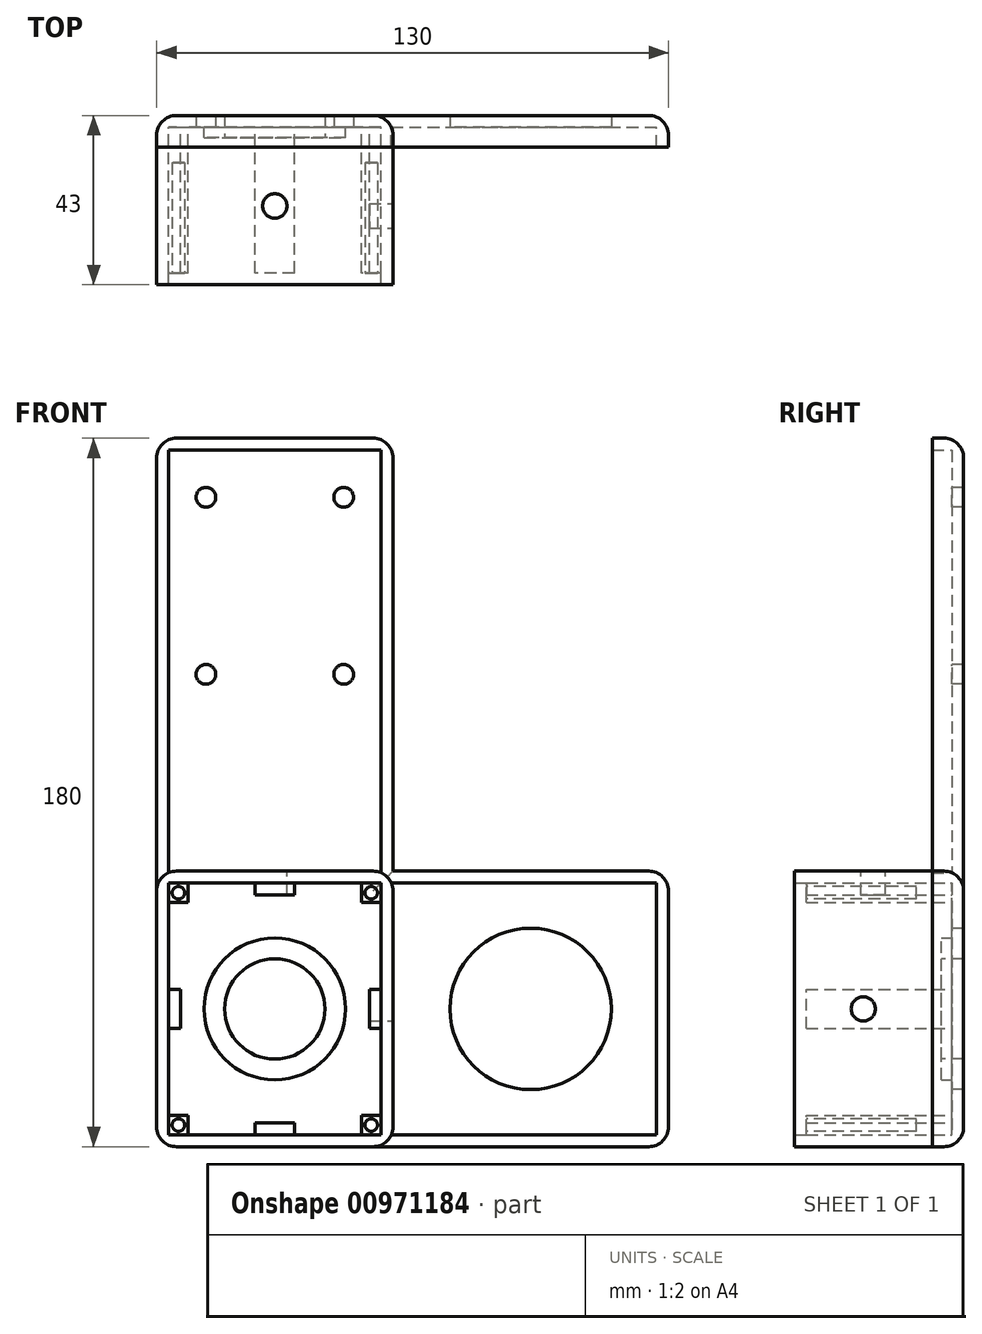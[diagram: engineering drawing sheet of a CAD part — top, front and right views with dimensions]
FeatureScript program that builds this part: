
annotation { "Feature Type Name" : "Feature", "Feature Type Description" : "" }
export const myFeature = defineFeature(function(context is Context, id is Id, definition is map)
    precondition{}
    {
        {
            var Q0;
            Q0=qCreatedBy(makeId("Front.planeOp"),FACE);
            var sketch = newSketch(context, id + "F0", { "sketchPlane" : qUnion([Q0])});
            skLineSegment(sketch, "E0.bottom", {"start": v(30, -90) * mm, "end": v(-30, -90) * mm});
            skLineSegment(sketch, "E0.top", {"start": v(30, 90) * mm, "end": v(-30, 90) * mm});
            skLineSegment(sketch, "E0.left", {"start": v(30, -90) * mm, "end": v(30, 90) * mm});
            skLineSegment(sketch, "E0.right", {"start": v(-30, -90) * mm, "end": v(-30, 90) * mm});
            skPoint(sketch, "E0.middle", {"position": v(0, 0) * mm});
            skCircle(sketch, "E1", {"center": v(0, -55) * mm, "radius": 12.75 * mm});
            skCircle(sketch, "E2", {"center": v(-17.5, 75) * mm, "radius": 2.5 * mm});
            skCircle(sketch, "E3", {"center": v(17.5, 75) * mm, "radius": 2.5 * mm});
            skCircle(sketch, "E4", {"center": v(-17.5, 30) * mm, "radius": 2.5 * mm});
            skCircle(sketch, "E5", {"center": v(17.5, 30) * mm, "radius": 2.5 * mm});
            skSolve(sketch);
        }
        {
            var Q0;
            Q0=makeQuery(id+"F0.imprint","IMPRINT",FACE,{"disambiguationData":[TD([[makeQuery(id+"F0.imprint","IMPRINT",EDGE,{"derivedFrom":sQuery(id+"F0.wireOp",EDGE,"E0.bottom")}),-1.0]])]});
            extrude(context, id + "F1", {"entities" : qUnion([Q0]), "oppositeDirection" : true, "depth" : 3 * mm, "offsetDistance" : 25 * mm});
        }
        {
            var Q0;
            Q0=makeQuery(id+"F1.opExtrude","CAP_FACE",FACE,{"disambiguationData":[OSD([sQuery(id+"F0.wireOp",EDGE,"E0.bottom"),sQuery(id+"F0.wireOp",EDGE,"E0.top"),sQuery(id+"F0.wireOp",EDGE,"E0.left"),sQuery(id+"F0.wireOp",EDGE,"E0.right"),sQuery(id+"F0.wireOp",EDGE,"E1")])],"isStart":true});
            var sketch = newSketch(context, id + "F2", { "sketchPlane" : qUnion([Q0])});
            skCircle(sketch, "E6", {"center": v(0, -55) * mm, "radius": 18 * mm});
            skSolve(sketch);
        }
        {
            var Q0;
            Q0=makeQuery(id+"F2.imprint","IMPRINT",FACE,{"disambiguationData":[TD([[makeQuery(id+"F2.imprint","IMPRINT",EDGE,{"derivedFrom":sQuery(id+"F2.wireOp",EDGE,"E6")}),1.0]])]});
            extrude(context, id + "F3", {"entities" : qUnion([Q0]), "operationType" : NewBodyOperationType.ADD, "depth" : 2.6 * mm, "offsetDistance" : 25 * mm});
        }
        {
            var Q0;
            Q0=makeQuery(id+"F1.opExtrude","CAP_FACE",FACE,{"disambiguationData":[OSD([sQuery(id+"F0.wireOp",EDGE,"E0.bottom"),sQuery(id+"F0.wireOp",EDGE,"E0.top"),sQuery(id+"F0.wireOp",EDGE,"E0.left"),sQuery(id+"F0.wireOp",EDGE,"E0.right"),sQuery(id+"F0.wireOp",EDGE,"E1")])],"isStart":true});
            var sketch = newSketch(context, id + "F4", { "sketchPlane" : qUnion([Q0])});
            skLineSegment(sketch, "E7.bottom", {"start": v(-30, -90) * mm, "end": v(30, -90) * mm});
            skLineSegment(sketch, "E7.top", {"start": v(-30, -20) * mm, "end": v(30, -20) * mm});
            skLineSegment(sketch, "E7.left", {"start": v(-30, -90) * mm, "end": v(-30, -20) * mm});
            skLineSegment(sketch, "E7.right", {"start": v(30, -90) * mm, "end": v(30, -20) * mm});
            skPoint(sketch, "E8", {"position": v(30, 0) * mm});
            skLineSegment(sketch, "E9", {"start": v(-27, -23) * mm, "end": v(27, -23) * mm});
            skLineSegment(sketch, "E10", {"start": v(27, -23) * mm, "end": v(27, -87) * mm});
            skLineSegment(sketch, "E11", {"start": v(27, -87) * mm, "end": v(-27, -87) * mm});
            skLineSegment(sketch, "E12", {"start": v(-27, -87) * mm, "end": v(-27, -23) * mm});
            skSolve(sketch);
        }
        {
            var Q0;
            Q0=makeQuery(id+"F4.imprint","IMPRINT",FACE,{"disambiguationData":[TD([[makeQuery(id+"F4.imprint","IMPRINT",EDGE,{"derivedFrom":sQuery(id+"F4.wireOp",EDGE,"E7.bottom")}),-1.0]])]});
            extrude(context, id + "F5", {"entities" : qUnion([Q0]), "operationType" : NewBodyOperationType.ADD, "depth" : 40 * mm, "offsetDistance" : 25 * mm});
        }
        {
            var Q0;
            Q0=makeQuery(id+"F5.boolean.opBoolean","SPLIT",FACE,{"disambiguationData":[TD([makeQuery(id+"F3.opExtrude","SWEPT_FACE",FACE,{"disambiguationData":[OSD([sQuery(id+"F2.wireOp",EDGE,"E6")])]})])],"derivedFrom":makeQuery(id+"F1.opExtrude","CAP_FACE",FACE,{"disambiguationData":[OSD([sQuery(id+"F0.wireOp",EDGE,"E0.bottom"),sQuery(id+"F0.wireOp",EDGE,"E0.top"),sQuery(id+"F0.wireOp",EDGE,"E0.left"),sQuery(id+"F0.wireOp",EDGE,"E0.right"),sQuery(id+"F0.wireOp",EDGE,"E1")])],"isStart":true})});
            var sketch = newSketch(context, id + "F6", { "sketchPlane" : qUnion([Q0])});
            skLineSegment(sketch, "E13.bottom", {"start": v(27, -23) * mm, "end": v(22, -23) * mm});
            skLineSegment(sketch, "E13.top", {"start": v(27, -28) * mm, "end": v(22, -28) * mm});
            skLineSegment(sketch, "E13.left", {"start": v(27, -23) * mm, "end": v(27, -28) * mm});
            skLineSegment(sketch, "E13.right", {"start": v(22, -23) * mm, "end": v(22, -28) * mm});
            skLineSegment(sketch, "E14.bottom", {"start": v(-27, -23) * mm, "end": v(-22, -23) * mm});
            skLineSegment(sketch, "E14.top", {"start": v(-27, -28) * mm, "end": v(-22, -28) * mm});
            skLineSegment(sketch, "E14.left", {"start": v(-27, -23) * mm, "end": v(-27, -28) * mm});
            skLineSegment(sketch, "E14.right", {"start": v(-22, -23) * mm, "end": v(-22, -28) * mm});
            skLineSegment(sketch, "E15.bottom", {"start": v(-27, -87) * mm, "end": v(-22, -87) * mm});
            skLineSegment(sketch, "E15.top", {"start": v(-27, -82) * mm, "end": v(-22, -82) * mm});
            skLineSegment(sketch, "E15.left", {"start": v(-27, -87) * mm, "end": v(-27, -82) * mm});
            skLineSegment(sketch, "E15.right", {"start": v(-22, -87) * mm, "end": v(-22, -82) * mm});
            skLineSegment(sketch, "E16.bottom", {"start": v(27, -87) * mm, "end": v(22, -87) * mm});
            skLineSegment(sketch, "E16.top", {"start": v(27, -82) * mm, "end": v(22, -82) * mm});
            skLineSegment(sketch, "E16.left", {"start": v(27, -87) * mm, "end": v(27, -82) * mm});
            skLineSegment(sketch, "E16.right", {"start": v(22, -87) * mm, "end": v(22, -82) * mm});
            skLineSegment(sketch, "E17.bottom", {"start": v(-5, -23) * mm, "end": v(5, -23) * mm});
            skLineSegment(sketch, "E17.top", {"start": v(-5, -26) * mm, "end": v(5, -26) * mm});
            skLineSegment(sketch, "E17.left", {"start": v(-5, -23) * mm, "end": v(-5, -26) * mm});
            skLineSegment(sketch, "E17.right", {"start": v(5, -23) * mm, "end": v(5, -26) * mm});
            skLineSegment(sketch, "E18.bottom", {"start": v(-5, -87) * mm, "end": v(5, -87) * mm});
            skLineSegment(sketch, "E18.top", {"start": v(-5, -84) * mm, "end": v(5, -84) * mm});
            skLineSegment(sketch, "E18.left", {"start": v(-5, -87) * mm, "end": v(-5, -84) * mm});
            skLineSegment(sketch, "E18.right", {"start": v(5, -87) * mm, "end": v(5, -84) * mm});
            skLineSegment(sketch, "E19.bottom", {"start": v(27, -50) * mm, "end": v(24, -50) * mm});
            skLineSegment(sketch, "E19.top", {"start": v(27, -60) * mm, "end": v(24, -60) * mm});
            skLineSegment(sketch, "E19.left", {"start": v(27, -50) * mm, "end": v(27, -60) * mm});
            skLineSegment(sketch, "E19.right", {"start": v(24, -50) * mm, "end": v(24, -60) * mm});
            skLineSegment(sketch, "E20.bottom", {"start": v(-27, -50) * mm, "end": v(-24, -50) * mm});
            skLineSegment(sketch, "E20.top", {"start": v(-27, -60) * mm, "end": v(-24, -60) * mm});
            skLineSegment(sketch, "E20.left", {"start": v(-27, -50) * mm, "end": v(-27, -60) * mm});
            skLineSegment(sketch, "E20.right", {"start": v(-24, -50) * mm, "end": v(-24, -60) * mm});
            skLineSegment(sketch, "E21", {"start": v(0, -33.43) * mm, "end": v(0, -77.94) * mm, "construction": true});
            skSolve(sketch);
        }
        {
            var Q0;
            Q0=makeQuery(id+"F6.imprint","IMPRINT",FACE,{"disambiguationData":[TD([[makeQuery(id+"F6.imprint","IMPRINT",EDGE,{"derivedFrom":sQuery(id+"F6.wireOp",EDGE,"E14.bottom")}),-1.0]])]});
            var Q1;
            Q1=makeQuery(id+"F6.imprint","IMPRINT",FACE,{"disambiguationData":[TD([[makeQuery(id+"F6.imprint","IMPRINT",EDGE,{"derivedFrom":sQuery(id+"F6.wireOp",EDGE,"E17.bottom")}),-1.0]])]});
            var Q2;
            Q2=makeQuery(id+"F6.imprint","IMPRINT",FACE,{"disambiguationData":[TD([[makeQuery(id+"F6.imprint","IMPRINT",EDGE,{"derivedFrom":sQuery(id+"F6.wireOp",EDGE,"E13.bottom")}),-1.0]])]});
            var Q3;
            Q3=makeQuery(id+"F6.imprint","IMPRINT",FACE,{"disambiguationData":[TD([[makeQuery(id+"F6.imprint","IMPRINT",EDGE,{"derivedFrom":sQuery(id+"F6.wireOp",EDGE,"E19.bottom")}),1.0]])]});
            var Q4;
            Q4=makeQuery(id+"F6.imprint","IMPRINT",FACE,{"disambiguationData":[TD([[makeQuery(id+"F6.imprint","IMPRINT",EDGE,{"derivedFrom":sQuery(id+"F6.wireOp",EDGE,"E20.bottom")}),-1.0]])]});
            var Q5;
            Q5=makeQuery(id+"F6.imprint","IMPRINT",FACE,{"disambiguationData":[TD([[makeQuery(id+"F6.imprint","IMPRINT",EDGE,{"derivedFrom":sQuery(id+"F6.wireOp",EDGE,"E16.bottom")}),-1.0]])]});
            var Q6;
            Q6=makeQuery(id+"F6.imprint","IMPRINT",FACE,{"disambiguationData":[TD([[makeQuery(id+"F6.imprint","IMPRINT",EDGE,{"derivedFrom":sQuery(id+"F6.wireOp",EDGE,"E18.bottom")}),-1.0]])]});
            var Q7;
            Q7=makeQuery(id+"F6.imprint","IMPRINT",FACE,{"disambiguationData":[TD([[makeQuery(id+"F6.imprint","IMPRINT",EDGE,{"derivedFrom":sQuery(id+"F6.wireOp",EDGE,"E15.bottom")}),-1.0]])]});
            extrude(context, id + "F7", {"entities" : qUnion([Q0, Q1, Q2, Q3, Q4, Q5, Q6, Q7]), "operationType" : NewBodyOperationType.ADD, "depth" : 37 * mm, "offsetDistance" : 25 * mm});
        }
        {
            var Q0;
            Q0=makeQuery(id+"F7.opExtrude","CAP_FACE",FACE,{"disambiguationData":[OSD([sQuery(id+"F6.wireOp",EDGE,"E13.bottom"),sQuery(id+"F6.wireOp",EDGE,"E13.top"),sQuery(id+"F6.wireOp",EDGE,"E13.left"),sQuery(id+"F6.wireOp",EDGE,"E13.right")])],"isStart":false});
            var sketch = newSketch(context, id + "F8", { "sketchPlane" : qUnion([Q0])});
            skCircle(sketch, "E22", {"center": v(24.5, -25.5) * mm, "radius": 1.6 * mm});
            skCircle(sketch, "E23", {"center": v(-24.5, -25.5) * mm, "radius": 1.6 * mm});
            skCircle(sketch, "E24", {"center": v(-24.5, -84.5) * mm, "radius": 1.6 * mm});
            skCircle(sketch, "E25", {"center": v(24.5, -84.5) * mm, "radius": 1.6 * mm});
            skSolve(sketch);
        }
        {
            var Q0;
            Q0=makeQuery(id+"F8.imprint","IMPRINT",FACE,{"disambiguationData":[TD([[makeQuery(id+"F8.imprint","IMPRINT",EDGE,{"derivedFrom":sQuery(id+"F8.wireOp",EDGE,"E22")}),1.0]])]});
            var Q1;
            Q1=makeQuery(id+"F8.imprint","IMPRINT",FACE,{"disambiguationData":[TD([[makeQuery(id+"F8.imprint","IMPRINT",EDGE,{"derivedFrom":sQuery(id+"F8.wireOp",EDGE,"E23")}),1.0]])]});
            var Q2;
            Q2=makeQuery(id+"F8.imprint","IMPRINT",FACE,{"disambiguationData":[TD([[makeQuery(id+"F8.imprint","IMPRINT",EDGE,{"derivedFrom":sQuery(id+"F8.wireOp",EDGE,"E25")}),1.0]])]});
            var Q3;
            Q3=makeQuery(id+"F8.imprint","IMPRINT",FACE,{"disambiguationData":[TD([[makeQuery(id+"F8.imprint","IMPRINT",EDGE,{"derivedFrom":sQuery(id+"F8.wireOp",EDGE,"E24")}),1.0]])]});
            extrude(context, id + "F9", {"entities" : qUnion([Q0, Q1, Q2, Q3]), "operationType" : NewBodyOperationType.REMOVE, "oppositeDirection" : true, "depth" : 28 * mm, "offsetDistance" : 25 * mm});
        }
        {
            var Q0;
            Q0=makeQuery(id+"F5.boolean.opBoolean","MERGE",FACE,{"derivedFrom":[makeQuery(id+"F1.opExtrude","SWEPT_FACE",FACE,{"disambiguationData":[OSD([sQuery(id+"F0.wireOp",EDGE,"E0.left")])]}),makeQuery(id+"F5.opExtrude","SWEPT_FACE",FACE,{"disambiguationData":[OSD([sQuery(id+"F4.wireOp",EDGE,"E7.right")])]})]});
            var sketch = newSketch(context, id + "F10", { "sketchPlane" : qUnion([Q0])});
            skLineSegment(sketch, "E26.bottom", {"start": v(3, -90) * mm, "end": v(0, -90) * mm});
            skLineSegment(sketch, "E26.top", {"start": v(3, -20) * mm, "end": v(0, -20) * mm});
            skLineSegment(sketch, "E26.left", {"start": v(3, -90) * mm, "end": v(3, -20) * mm});
            skLineSegment(sketch, "E26.right", {"start": v(0, -90) * mm, "end": v(0, -20) * mm});
            skSolve(sketch);
        }
        {
            var Q0;
            Q0=makeQuery(id+"F10.imprint","IMPRINT",FACE,{"disambiguationData":[TD([[makeQuery(id+"F10.imprint","IMPRINT",EDGE,{"derivedFrom":sQuery(id+"F10.wireOp",EDGE,"E26.bottom")}),-1.0]])]});
            extrude(context, id + "F11", {"entities" : qUnion([Q0]), "operationType" : NewBodyOperationType.ADD, "depth" : 70 * mm, "offsetDistance" : 25 * mm});
        }
        {
            var Q0;
            Q0=makeQuery(id+"F11.opExtrude","SWEPT_FACE",FACE,{"disambiguationData":[OSD([sQuery(id+"F10.wireOp",EDGE,"E26.right")])]});
            var sketch = newSketch(context, id + "F12", { "sketchPlane" : qUnion([Q0])});
            skLineSegment(sketch, "E27", {"start": v(30, -55) * mm, "end": v(128.66, -55) * mm, "construction": true});
            skPoint(sketch, "E27.endSnap0", {"position": v(100, -55) * mm});
            skLineSegment(sketch, "E28", {"start": v(65, 0) * mm, "end": v(65, -99.6) * mm, "construction": true});
            skPoint(sketch, "E28.startSnap0", {"position": v(65, -20) * mm});
            skSolve(sketch);
        }
        {
            var Q0;
            {var subQ0=sQuery(id+"F10.wireOp",EDGE,"E26.right");Q0=makeQuery(id+"F12.imprint","IMPRINT",FACE,{"disambiguationData":[TD([[makeQuery(id+"F12.imprint","IMPRINT",EDGE,{"derivedFrom":makeQuery(id+"F11.opExtrude","CAP_EDGE",EDGE,{"disambiguationData":[OSD([subQ0])],"isStart":false})}),1.0]])]});}
            var sketch = newSketch(context, id + "F13", { "sketchPlane" : qUnion([Q0])});
            skCircle(sketch, "E29", {"center": v(65, -55) * mm, "radius": 20.5 * mm});
            skSolve(sketch);
        }
        {
            var Q0;
            Q0=makeQuery(id+"F13.imprint","IMPRINT",FACE,{"disambiguationData":[TD([[makeQuery(id+"F13.imprint","IMPRINT",EDGE,{"derivedFrom":sQuery(id+"F13.wireOp",EDGE,"E29")}),1.0]])]});
            extrude(context, id + "F14", {"entities" : qUnion([Q0]), "operationType" : NewBodyOperationType.REMOVE, "endBound" : BoundingType.UP_TO_NEXT, "oppositeDirection" : true, "depth" : 25 * mm, "offsetDistance" : 25 * mm});
        }
        {
            var Q0;
            {var subQ0=sQuery(id+"F10.wireOp",EDGE,"E26.right");Q0=makeQuery(id+"F12.imprint","IMPRINT",FACE,{"disambiguationData":[TD([[makeQuery(id+"F12.imprint","IMPRINT",EDGE,{"derivedFrom":makeQuery(id+"F11.opExtrude","CAP_EDGE",EDGE,{"disambiguationData":[OSD([subQ0])],"isStart":false})}),1.0]])]});}
            var sketch = newSketch(context, id + "F15", { "sketchPlane" : qUnion([Q0])});
            skLineSegment(sketch, "E30.bottom", {"start": v(30, -20) * mm, "end": v(100, -20) * mm});
            skLineSegment(sketch, "E30.top", {"start": v(30, -23) * mm, "end": v(97, -23) * mm});
            skLineSegment(sketch, "E30.left", {"start": v(30, -20) * mm, "end": v(30, -23) * mm});
            skLineSegment(sketch, "E30.right", {"start": v(100, -20) * mm, "end": v(100, -23) * mm});
            skLineSegment(sketch, "E31.bottom", {"start": v(30, -87) * mm, "end": v(97, -87) * mm});
            skLineSegment(sketch, "E31.top", {"start": v(30, -90) * mm, "end": v(100, -90) * mm});
            skLineSegment(sketch, "E31.left", {"start": v(30, -87) * mm, "end": v(30, -90) * mm});
            skLineSegment(sketch, "E31.right", {"start": v(100, -87) * mm, "end": v(100, -90) * mm});
            skLineSegment(sketch, "E32.left", {"start": v(100, -23) * mm, "end": v(100, -87) * mm});
            skLineSegment(sketch, "E32.right", {"start": v(97, -23) * mm, "end": v(97, -87) * mm});
            skSolve(sketch);
        }
        {
            var Q0;
            Q0=makeQuery(id+"F15.imprint","IMPRINT",FACE,{"disambiguationData":[TD([[makeQuery(id+"F15.imprint","IMPRINT",EDGE,{"derivedFrom":sQuery(id+"F15.wireOp",EDGE,"E30.bottom")}),1.0]])]});
            extrude(context, id + "F16", {"entities" : qUnion([Q0]), "operationType" : NewBodyOperationType.ADD, "depth" : 5 * mm, "offsetDistance" : 25 * mm});
        }
        {
            var Q0;
            {var subQ1=sQuery(id+"F0.wireOp",EDGE,"E0.left");var subQ2=makeQuery(id+"F1.opExtrude","SWEPT_FACE",FACE,{"disambiguationData":[OSD([subQ1])]});var subQ3=sQuery(id+"F0.wireOp",EDGE,"E0.bottom");var subQ4=sQuery(id+"F4.wireOp",EDGE,"E7.right");var subQ5=makeQuery(id+"F5.opExtrude","SWEPT_FACE",FACE,{"disambiguationData":[OSD([subQ4])]});Q0=makeQuery(id+"F11.boolean.opBoolean","SPLIT",FACE,{"disambiguationData":[TD([makeQuery(id+"F1.opExtrude","SWEPT_FACE",FACE,{"disambiguationData":[OSD([subQ3])]})])],"derivedFrom":makeQuery(id+"F5.boolean.opBoolean","MERGE",FACE,{"derivedFrom":[subQ2,subQ5]})});}
            var sketch = newSketch(context, id + "F17", { "sketchPlane" : qUnion([Q0])});
            skCircle(sketch, "E33", {"center": v(-22.5, -55) * mm, "radius": 3.07 * mm});
            skPoint(sketch, "E33.centerSnap0", {"position": v(-22.5, -20) * mm});
            skSolve(sketch);
        }
        {
            var Q0;
            Q0=makeQuery(id+"F17.imprint","IMPRINT",FACE,{"disambiguationData":[TD([[makeQuery(id+"F17.imprint","IMPRINT",EDGE,{"derivedFrom":sQuery(id+"F17.wireOp",EDGE,"E33")}),1.0]])]});
            extrude(context, id + "F18", {"entities" : qUnion([Q0]), "operationType" : NewBodyOperationType.REMOVE, "endBound" : BoundingType.UP_TO_NEXT, "oppositeDirection" : true, "depth" : 25 * mm, "offsetDistance" : 25 * mm});
        }
        {
            var Q0;
            Q0=makeQuery(id+"F16.boolean.opBoolean","MERGE",FACE,{"derivedFrom":[makeQuery(id+"F5.opExtrude","SWEPT_FACE",FACE,{"disambiguationData":[OSD([sQuery(id+"F4.wireOp",EDGE,"E7.top")])]}),makeQuery(id+"F11.opExtrude","SWEPT_FACE",FACE,{"disambiguationData":[OSD([sQuery(id+"F10.wireOp",EDGE,"E26.top")])]}),makeQuery(id+"F16.opExtrude","SWEPT_FACE",FACE,{"disambiguationData":[OSD([sQuery(id+"F15.wireOp",EDGE,"E30.bottom")])]})]});
            var sketch = newSketch(context, id + "F19", { "sketchPlane" : qUnion([Q0])});
            skCircle(sketch, "E34", {"center": v(0, -20) * mm, "radius": 3.1 * mm});
            skPoint(sketch, "E34.centerSnap0", {"position": v(-30, -20) * mm});
            skSolve(sketch);
        }
        {
            var Q0;
            Q0=makeQuery(id+"F19.imprint","IMPRINT",FACE,{"disambiguationData":[TD([[makeQuery(id+"F19.imprint","IMPRINT",EDGE,{"derivedFrom":sQuery(id+"F19.wireOp",EDGE,"E34")}),1.0]])]});
            extrude(context, id + "F20", {"entities" : qUnion([Q0]), "operationType" : NewBodyOperationType.REMOVE, "endBound" : BoundingType.UP_TO_NEXT, "oppositeDirection" : true, "depth" : 25 * mm, "offsetDistance" : 25 * mm});
        }
        {
            var Q0;
            {var subQ0=sQuery(id+"F0.wireOp",EDGE,"E0.right");var subQ1=sQuery(id+"F0.wireOp",EDGE,"E0.left");var subQ2=sQuery(id+"F0.wireOp",EDGE,"E0.top");Q0=makeQuery(id+"F5.boolean.opBoolean","SPLIT",FACE,{"disambiguationData":[TD([makeQuery(id+"F1.opExtrude","SWEPT_FACE",FACE,{"disambiguationData":[OSD([subQ2])]})])],"derivedFrom":makeQuery(id+"F1.opExtrude","CAP_FACE",FACE,{"disambiguationData":[OSD([sQuery(id+"F0.wireOp",EDGE,"E0.bottom"),subQ2,subQ1,subQ0,sQuery(id+"F0.wireOp",EDGE,"E1")])],"isStart":true})});}
            var sketch = newSketch(context, id + "F21", { "sketchPlane" : qUnion([Q0])});
            skLineSegment(sketch, "E35.bottom", {"start": v(30, 90) * mm, "end": v(27, 90) * mm});
            skLineSegment(sketch, "E35.top", {"start": v(30, -20) * mm, "end": v(27, -20) * mm});
            skLineSegment(sketch, "E35.left", {"start": v(30, 90) * mm, "end": v(30, -20) * mm});
            skLineSegment(sketch, "E35.right", {"start": v(27, 87) * mm, "end": v(27, -20) * mm});
            skLineSegment(sketch, "E36.bottom", {"start": v(-30, 90) * mm, "end": v(-27, 90) * mm});
            skLineSegment(sketch, "E36.top", {"start": v(-30, -20) * mm, "end": v(-27, -20) * mm});
            skLineSegment(sketch, "E36.left", {"start": v(-30, 90) * mm, "end": v(-30, -20) * mm});
            skLineSegment(sketch, "E36.right", {"start": v(-27, 87) * mm, "end": v(-27, -20) * mm});
            skLineSegment(sketch, "E37.bottom", {"start": v(-27, 90) * mm, "end": v(21.68, 90) * mm});
            skLineSegment(sketch, "E37.top", {"start": v(-27, 87) * mm, "end": v(27, 87) * mm});
            skSolve(sketch);
        }
        {
            var Q0;
            {var subQ1=sQuery(id+"F21.wireOp",EDGE,"E35.bottom");Q0=makeQuery(id+"F21.imprint","IMPRINT",FACE,{"disambiguationData":[TD([[makeQuery(id+"F21.imprint","IMPRINT",EDGE,{"derivedFrom":subQ1}),1.0]])]});}
            extrude(context, id + "F22", {"entities" : qUnion([Q0]), "operationType" : NewBodyOperationType.ADD, "depth" : 5 * mm, "offsetDistance" : 25 * mm});
        }
        {
            var Q0;
            Q0=makeQuery(id+"F11.boolean.opBoolean","MERGE",EDGE,{"derivedFrom":[makeQuery(id+"F1.opExtrude","CAP_EDGE",EDGE,{"disambiguationData":[OSD([sQuery(id+"F0.wireOp",EDGE,"E0.bottom")])],"isStart":false}),makeQuery(id+"F11.opExtrude","SWEPT_EDGE",EDGE,{"disambiguationData":[OSD([sQuery(id+"F10.wireOp",EDGE,"E26.bottom"),sQuery(id+"F10.wireOp",EDGE,"E26.left")])]})]});
            var Q1;
            Q1=makeQuery(id+"F1.opExtrude","CAP_EDGE",EDGE,{"disambiguationData":[OSD([sQuery(id+"F0.wireOp",EDGE,"E0.right")])],"isStart":false});
            var Q2;
            Q2=makeQuery(id+"F1.opExtrude","CAP_EDGE",EDGE,{"disambiguationData":[OSD([sQuery(id+"F0.wireOp",EDGE,"E0.top")])],"isStart":false});
            var Q3;
            Q3=makeQuery(id+"F1.opExtrude","CAP_EDGE",EDGE,{"disambiguationData":[OSD([sQuery(id+"F0.wireOp",EDGE,"E0.left")])],"isStart":false});
            var Q4;
            Q4=makeQuery(id+"F11.opExtrude","SWEPT_EDGE",EDGE,{"disambiguationData":[OSD([sQuery(id+"F0.wireOp",EDGE,"E0.left"),sQuery(id+"F10.wireOp",EDGE,"E26.top"),sQuery(id+"F10.wireOp",EDGE,"E26.left")])]});
            var Q5;
            Q5=makeQuery(id+"F11.opExtrude","CAP_EDGE",EDGE,{"disambiguationData":[OSD([sQuery(id+"F10.wireOp",EDGE,"E26.left")])],"isStart":false});
            fillet(context, id + "F23", {"entities" : qUnion([Q0, Q1, Q2, Q3, Q4, Q5]), "radius" : 5 * mm, "tangentPropagation" : true, "allowEdgeOverflow" : false});
        }
        {
            var Q0;
            Q0=makeQuery(id+"F5.opExtrude","SWEPT_EDGE",EDGE,{"disambiguationData":[OSD([sQuery(id+"F0.wireOp",EDGE,"E0.left"),sQuery(id+"F4.wireOp",EDGE,"E7.top"),sQuery(id+"F4.wireOp",EDGE,"E7.right")])]});
            var Q1;
            Q1=makeQuery(id+"F5.opExtrude","SWEPT_EDGE",EDGE,{"disambiguationData":[OSD([sQuery(id+"F0.wireOp",EDGE,"E0.right"),sQuery(id+"F4.wireOp",EDGE,"E7.top"),sQuery(id+"F4.wireOp",EDGE,"E7.left")])]});
            var Q2;
            Q2=makeQuery(id+"F5.boolean.opBoolean","MERGE",EDGE,{"derivedFrom":[makeQuery(id+"F1.opExtrude","SWEPT_EDGE",EDGE,{"disambiguationData":[OSD([sQuery(id+"F0.wireOp",EDGE,"E0.bottom"),sQuery(id+"F0.wireOp",EDGE,"E0.left")])]}),makeQuery(id+"F5.opExtrude","SWEPT_EDGE",EDGE,{"disambiguationData":[OSD([sQuery(id+"F4.wireOp",EDGE,"E7.bottom"),sQuery(id+"F4.wireOp",EDGE,"E7.right")])]})]});
            var Q3;
            Q3=makeQuery(id+"F5.boolean.opBoolean","MERGE",EDGE,{"derivedFrom":[makeQuery(id+"F1.opExtrude","SWEPT_EDGE",EDGE,{"disambiguationData":[OSD([sQuery(id+"F0.wireOp",EDGE,"E0.bottom"),sQuery(id+"F0.wireOp",EDGE,"E0.right")])]}),makeQuery(id+"F5.opExtrude","SWEPT_EDGE",EDGE,{"disambiguationData":[OSD([sQuery(id+"F4.wireOp",EDGE,"E7.bottom"),sQuery(id+"F4.wireOp",EDGE,"E7.left")])]})]});
            var Q4;
            Q4=makeQuery(id+"F16.boolean.opBoolean","MERGE",EDGE,{"derivedFrom":[makeQuery(id+"F11.opExtrude","CAP_EDGE",EDGE,{"disambiguationData":[OSD([sQuery(id+"F10.wireOp",EDGE,"E26.top")])],"isStart":false}),makeQuery(id+"F16.opExtrude","SWEPT_EDGE",EDGE,{"disambiguationData":[OSD([sQuery(id+"F15.wireOp",EDGE,"E30.bottom"),sQuery(id+"F15.wireOp",EDGE,"E30.right")])]})]});
            var Q5;
            Q5=makeQuery(id+"F16.boolean.opBoolean","MERGE",EDGE,{"derivedFrom":[makeQuery(id+"F11.opExtrude","CAP_EDGE",EDGE,{"disambiguationData":[OSD([sQuery(id+"F10.wireOp",EDGE,"E26.bottom")])],"isStart":false}),makeQuery(id+"F16.opExtrude","SWEPT_EDGE",EDGE,{"disambiguationData":[OSD([sQuery(id+"F15.wireOp",EDGE,"E31.top"),sQuery(id+"F15.wireOp",EDGE,"E31.right")])]})]});
            var Q6;
            Q6=makeQuery(id+"F22.boolean.opBoolean","MERGE",EDGE,{"derivedFrom":[makeQuery(id+"F1.opExtrude","SWEPT_EDGE",EDGE,{"disambiguationData":[OSD([sQuery(id+"F0.wireOp",EDGE,"E0.top"),sQuery(id+"F0.wireOp",EDGE,"E0.left")])]}),makeQuery(id+"F22.opExtrude","SWEPT_EDGE",EDGE,{"disambiguationData":[OSD([sQuery(id+"F21.wireOp",EDGE,"E35.bottom"),sQuery(id+"F21.wireOp",EDGE,"E35.left")])]})]});
            var Q7;
            Q7=makeQuery(id+"F22.boolean.opBoolean","MERGE",EDGE,{"derivedFrom":[makeQuery(id+"F1.opExtrude","SWEPT_EDGE",EDGE,{"disambiguationData":[OSD([sQuery(id+"F0.wireOp",EDGE,"E0.top"),sQuery(id+"F0.wireOp",EDGE,"E0.right")])]}),makeQuery(id+"F22.opExtrude","SWEPT_EDGE",EDGE,{"disambiguationData":[OSD([sQuery(id+"F21.wireOp",EDGE,"E36.bottom"),sQuery(id+"F21.wireOp",EDGE,"E36.left")])]})]});
            fillet(context, id + "F24", {"entities" : qUnion([Q0, Q1, Q2, Q3, Q4, Q5, Q6, Q7]), "radius" : 5 * mm, "tangentPropagation" : true, "allowEdgeOverflow" : false});
        }
    });
